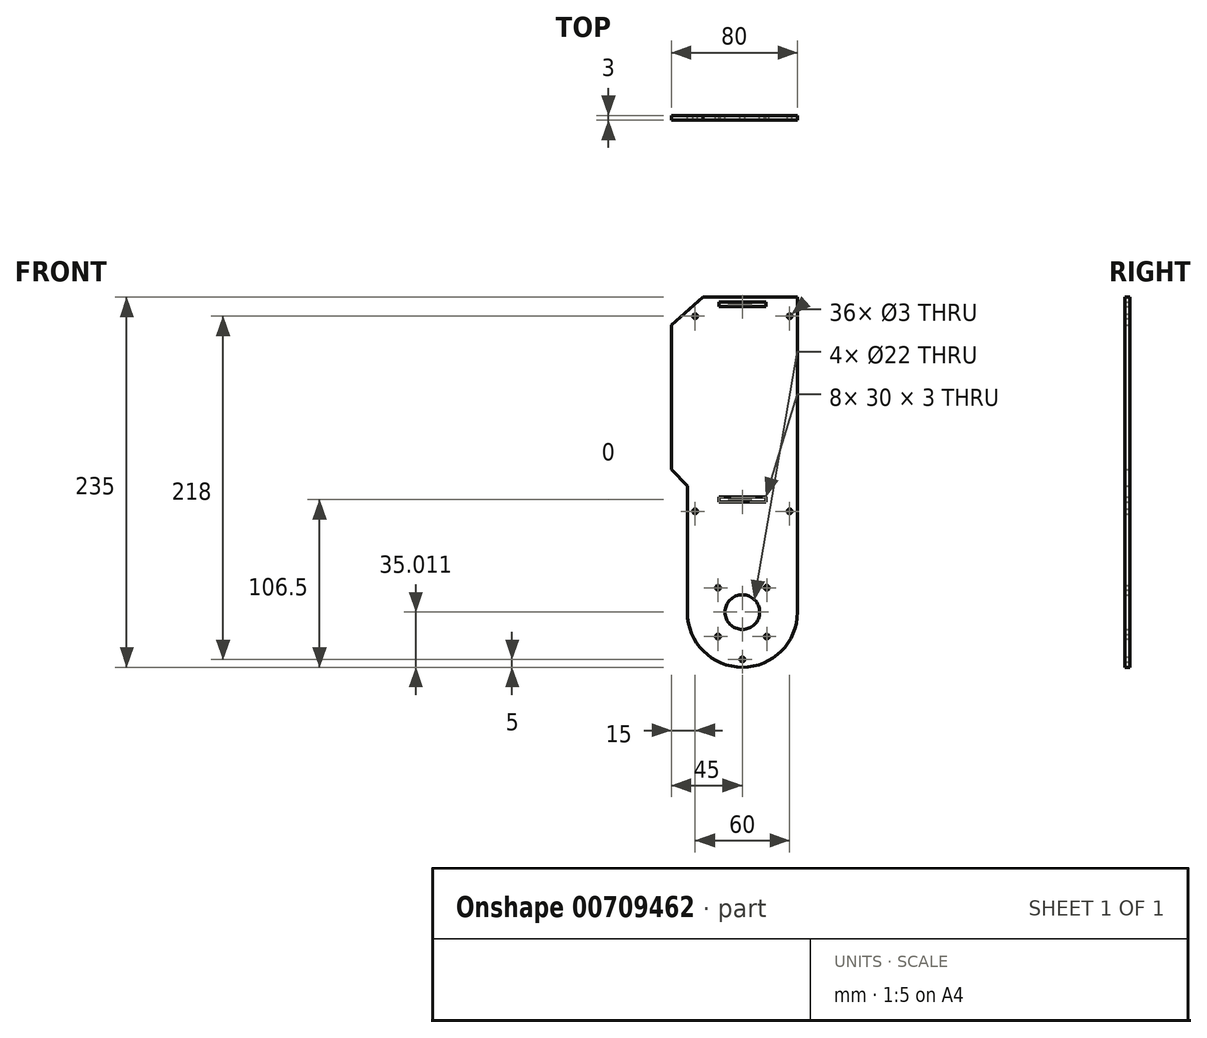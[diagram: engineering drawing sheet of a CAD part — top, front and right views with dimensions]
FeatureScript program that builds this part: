
annotation { "Feature Type Name" : "Feature", "Feature Type Description" : "" }
export const myFeature = defineFeature(function(context is Context, id is Id, definition is map)
    precondition{}
    {
        {
            var Q0;
            Q0=qCreatedBy(makeId("Front.planeOp"),FACE);
            var sketch = newSketch(context, id + "F0", { "sketchPlane" : qUnion([Q0])});
            skLineSegment(sketch, "E0.right", {"start": v(35, 100) * mm, "end": v(35, -100) * mm});
            skPoint(sketch, "E0.middle", {"position": v(0, 0) * mm});
            skLineSegment(sketch, "E1", {"start": v(-35, -100) * mm, "end": v(35, -100) * mm});
            skCircle(sketch, "E2", {"center": v(0, -100) * mm, "radius": 35 * mm});
            skPoint(sketch, "E3", {"position": v(-25, 100) * mm});
            skLineSegment(sketch, "E4", {"start": v(-25, 100) * mm, "end": v(-45, 82.5) * mm});
            skLineSegment(sketch, "E5", {"start": v(35, 100) * mm, "end": v(-25, 100) * mm});
            skCircle(sketch, "E6", {"center": v(0, -99.99) * mm, "radius": 11 * mm});
            skCircle(sketch, "E7", {"center": v(15.5, -84.5) * mm, "radius": 1.5 * mm});
            skCircle(sketch, "E8.MirrorC", {"center": v(15.5, -115.5) * mm, "radius": 1.5 * mm});
            skCircle(sketch, "E9.MirrorC", {"center": v(-15.5, -84.5) * mm, "radius": 1.5 * mm});
            skCircle(sketch, "E10.MirrorC", {"center": v(-15.5, -115.5) * mm, "radius": 1.5 * mm});
            skPoint(sketch, "E11", {"position": v(-35, -20) * mm});
            skLineSegment(sketch, "E12", {"start": v(-45, -9.33) * mm, "end": v(-35, -20) * mm});
            skLineSegment(sketch, "E13", {"start": v(-35, -20) * mm, "end": v(-35, -100) * mm});
            skLineSegment(sketch, "E14", {"start": v(-45, 82.5) * mm, "end": v(-45, -9.33) * mm});
            skCircle(sketch, "E15", {"center": v(0, -130) * mm, "radius": 1.5 * mm});
            skLineSegment(sketch, "E16.bottom", {"start": v(-15, -27) * mm, "end": v(15, -27) * mm});
            skLineSegment(sketch, "E16.top", {"start": v(-15, -30) * mm, "end": v(15, -30) * mm});
            skLineSegment(sketch, "E16.left", {"start": v(-15, -27) * mm, "end": v(-15, -30) * mm});
            skLineSegment(sketch, "E16.right", {"start": v(15, -27) * mm, "end": v(15, -30) * mm});
            skCircle(sketch, "E17", {"center": v(-30, -36) * mm, "radius": 1.5 * mm});
            skCircle(sketch, "E18.MirrorC", {"center": v(30, -36) * mm, "radius": 1.5 * mm});
            skLineSegment(sketch, "E19.bottom", {"start": v(-15, 97) * mm, "end": v(15, 97) * mm});
            skLineSegment(sketch, "E19.top", {"start": v(-15, 94) * mm, "end": v(15, 94) * mm});
            skLineSegment(sketch, "E19.left", {"start": v(-15, 97) * mm, "end": v(-15, 94) * mm});
            skLineSegment(sketch, "E19.right", {"start": v(15, 97) * mm, "end": v(15, 94) * mm});
            skCircle(sketch, "E20.MirrorC", {"center": v(30, 88) * mm, "radius": 1.5 * mm});
            skCircle(sketch, "E21", {"center": v(-30, 88) * mm, "radius": 1.5 * mm});
            skSolve(sketch);
        }
        {
            var Q0;
            Q0 = qSketchRegion(id + "F0", true);
            extrude(context, id + "F1", {"entities" : qUnion([Q0]), "depth" : 3 * mm, "offsetDistance" : 25 * mm});
        }
    });
